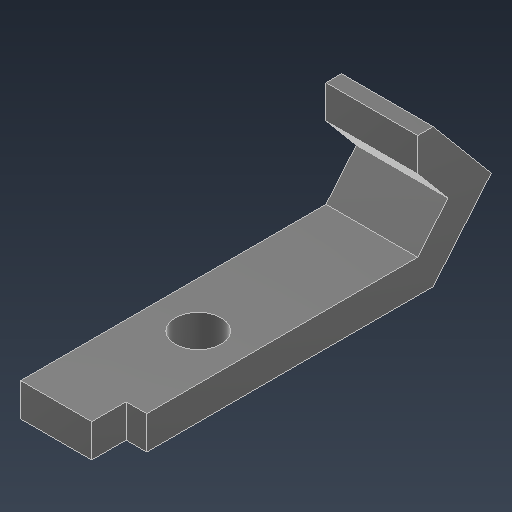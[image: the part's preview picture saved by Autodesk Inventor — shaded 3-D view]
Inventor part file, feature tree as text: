
AUTODESK INVENTOR PART (.ipt)
format: ipt  version: 2021.3 (Build 253353000, 353)  size: 119,296 bytes
history: native  units: mm
features: extrude x3, sketch x3
ambient origin geometry x8: Origin, YZ Plane, XZ Plane, XY Plane, X Axis, Y Axis, Z Axis, Center Point
bodies: Solid1 (feature_tree)
feature tree (6):
  extrude  "Extrusion1"  Depth=25.0mm
  extrude  "Extrusion2"  Depth=3.15mm
  extrude  "Extrusion3"  Depth=3.0mm
  sketch  "Sketch1"  dims[d0=2.9mm d1=25.0mm]
  sketch  "Sketch2"  dims[d2=8.726646mm d3=3.15mm]
  sketch  "Sketch3"  dims[d4=2.9mm d5=8.726646mm d6=3.15mm d8=8.0mm d9=0.0mm d11=6.2mm d12=3.0mm d13=0.0mm d14=8.5mm d15=4.0mm d16=0.0mm d17=0.0mm]
